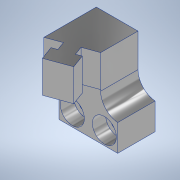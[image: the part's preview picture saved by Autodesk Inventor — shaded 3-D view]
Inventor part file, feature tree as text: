
AUTODESK INVENTOR PART (.ipt)
format: ipt  version: 2022 (Build 260153000, 153)  size: 187,392 bytes
history: native  units: mm
features: sketch x7, extrude x6, other x3, fillet x1
ambient origin geometry x8: Origin, YZ Plane, XZ Plane, XY Plane, X Axis, Y Axis, Z Axis, Center Point
bodies: Solid1 (feature_tree)
feature tree (17):
  other  "Mono_20deg.iam"
  other  "Anschluss_Finger_20deg.ipt:1"
  other  "Anschluss_Greifer.ipt:1"
  extrude  "Extrusion1"  Depth=10.0mm TaperAngle=0.0deg
  extrude  "Extrusion2"  Depth=9.0mm
  fillet  "Fillet1"  Radius=4.0mm
  extrude  "Extrusion3"  Depth=10.0mm
  extrude  "Extrusion4"  Depth=9.0mm
  extrude  "Extrusion5"  Depth=5.0mm TaperAngle=0.0deg
  extrude  "Extrusion6"  [1 undecoded]
  sketch  "Sketch4"  dims[d7=7.0mm d8=10.0mm]
  sketch  "Sketch2"  dims[d0=10.0mm d1=4.0mm d2=0.0mm]
  sketch  "Sketch3"  dims[d3=9.0mm d4=9.0mm d5=4.0mm d6=0.0mm]
  sketch  "Sketch5"  dims[d9=4.0mm d10=0.0mm d11=9.0mm]
  sketch  "Sketch6"  dims[d12=4.0mm d13=0.0mm d14=5.0mm d15=0.0mm]
  sketch  "Sketch7"  dims[d16=0.0mm d17=0.0mm]
  sketch  "Sketch8"
note: 1 required parameter value undecoded (feature->parameter linkage not recoverable at this tier; creation-order binding heuristic only, values carry confidence <= 0.55)
